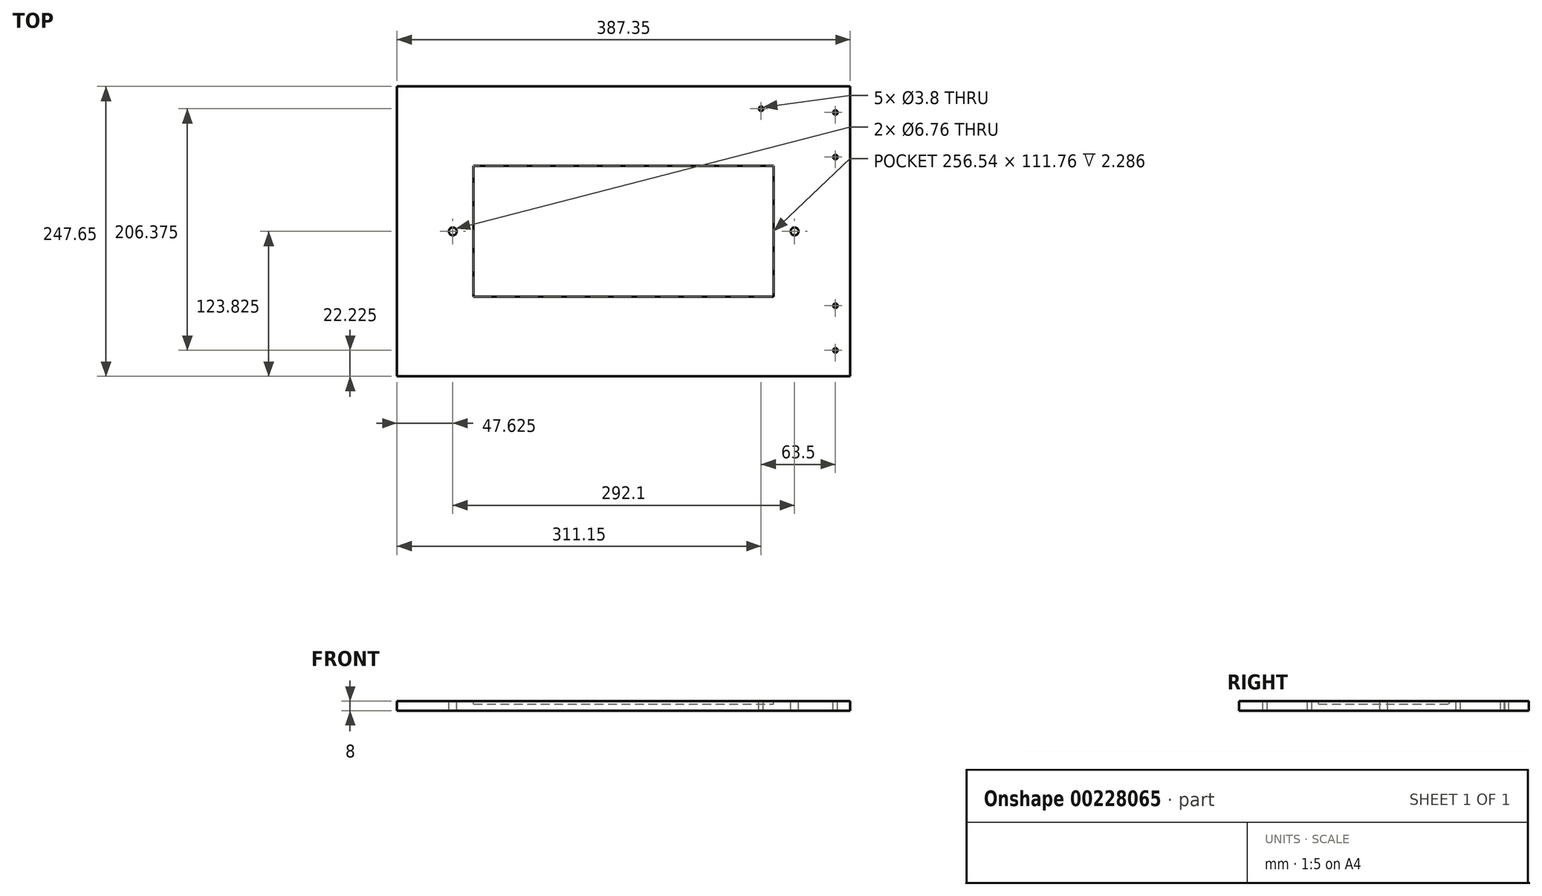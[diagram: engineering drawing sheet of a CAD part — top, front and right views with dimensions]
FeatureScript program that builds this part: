
annotation { "Feature Type Name" : "Feature", "Feature Type Description" : "" }
export const myFeature = defineFeature(function(context is Context, id is Id, definition is map)
    precondition{}
    {
        {
            var Q0;
            Q0=qCreatedBy(makeId("Top.planeOp"),FACE);
            var sketch = newSketch(context, id + "F0", { "sketchPlane" : qUnion([Q0])});
            skLineSegment(sketch, "E0.bottom", {"start": v(0, 0) * mm, "end": v(387.35, 0) * mm});
            skLineSegment(sketch, "E0.top", {"start": v(0, 247.65) * mm, "end": v(387.35, 247.65) * mm});
            skLineSegment(sketch, "E0.left", {"start": v(0, 0) * mm, "end": v(0, 247.65) * mm});
            skLineSegment(sketch, "E0.right", {"start": v(387.35, 0) * mm, "end": v(387.35, 247.65) * mm});
            skSolve(sketch);
        }
        {
            var Q0;
            Q0 = qSketchRegion(id + "F0", true);
            extrude(context, id + "F1", {"entities" : qUnion([Q0]), "depth" : 8 * mm});
        }
        {
            var Q0;
            Q0=makeQuery(id+"F1.opExtrude","CAP_FACE",FACE,{"disambiguationData":[OSD([sQuery(id+"F0.wireOp",EDGE,"E0.bottom"),sQuery(id+"F0.wireOp",EDGE,"E0.top"),sQuery(id+"F0.wireOp",EDGE,"E0.left"),sQuery(id+"F0.wireOp",EDGE,"E0.right")])],"isStart":false});
            var sketch = newSketch(context, id + "F2", { "sketchPlane" : qUnion([Q0])});
            skPoint(sketch, "E1", {"position": v(374.65, 225.43) * mm});
            skPoint(sketch, "E2", {"position": v(374.65, 187.33) * mm});
            skPoint(sketch, "E3", {"position": v(374.65, 60.33) * mm});
            skPoint(sketch, "E4", {"position": v(374.65, 22.23) * mm});
            skLineSegment(sketch, "E5", {"start": v(374.65, 225.43) * mm, "end": v(374.65, 247.65) * mm, "construction": true});
            skLineSegment(sketch, "E6", {"start": v(374.65, 22.23) * mm, "end": v(374.65, 0) * mm, "construction": true});
            skSolve(sketch);
        }
        {
            var Q0;
            Q0=sQuery(id+"F2.wireOp",VERTEX,"E1");
            var Q1;
            Q1=sQuery(id+"F2.wireOp",VERTEX,"E2");
            var Q2;
            Q2=sQuery(id+"F2.wireOp",VERTEX,"E3");
            var Q3;
            Q3=sQuery(id+"F2.wireOp",VERTEX,"E4");
            var Q4;
            Q4=makeQuery(id+"F1.opExtrude","SWEPT_BODY",BODY,{"disambiguationData":[OSD([sQuery(id+"F0.wireOp",EDGE,"E0.bottom"),sQuery(id+"F0.wireOp",EDGE,"E0.top"),sQuery(id+"F0.wireOp",EDGE,"E0.left"),sQuery(id+"F0.wireOp",EDGE,"E0.right")])]});
            hole(context, id + "F3", {"style" : HoleStyle.SIMPLE, "endStyle" : HoleEndStyle.THROUGH, "standardTappedOrClearance" : lookupTablePath({ "standard" : "ANSI", "fit" : "Normal (ASME)", "size" : "#6", "type" : "Clearance" }), "standardBlindInLast" : lookupTablePath({ "fit" : "Free", "standard" : "ANSI", "size" : "#6", "type" : "Clearance" }), "holeDiameter" : 3.8 * mm, "locations" : qUnion([Q0, Q1, Q2, Q3]), "scope" : qUnion([Q4]), "isTappedThrough" : true});
        }
        {
            var Q0;
            Q0=makeQuery(id+"F1.opExtrude","CAP_FACE",FACE,{"disambiguationData":[OSD([sQuery(id+"F0.wireOp",EDGE,"E0.bottom"),sQuery(id+"F0.wireOp",EDGE,"E0.top"),sQuery(id+"F0.wireOp",EDGE,"E0.left"),sQuery(id+"F0.wireOp",EDGE,"E0.right")])],"isStart":false});
            var sketch = newSketch(context, id + "F4", { "sketchPlane" : qUnion([Q0])});
            skPoint(sketch, "E7", {"position": v(47.62, 123.83) * mm});
            skPoint(sketch, "E8", {"position": v(339.73, 123.83) * mm});
            skLineSegment(sketch, "E9", {"start": v(47.62, 247.65) * mm, "end": v(47.62, 0) * mm, "construction": true});
            skLineSegment(sketch, "E10", {"start": v(339.73, 247.65) * mm, "end": v(339.73, 0) * mm, "construction": true});
            skLineSegment(sketch, "E11", {"start": v(0, 123.83) * mm, "end": v(47.62, 123.83) * mm, "construction": true});
            skLineSegment(sketch, "E12", {"start": v(339.73, 123.83) * mm, "end": v(387.35, 123.83) * mm, "construction": true});
            skSolve(sketch);
        }
        {
            var Q0;
            Q0=sQuery(id+"F4.wireOp",VERTEX,"E7");
            var Q1;
            Q1=sQuery(id+"F4.wireOp",VERTEX,"E8");
            var Q2;
            Q2=makeQuery(id+"F1.opExtrude","SWEPT_BODY",BODY,{"disambiguationData":[OSD([sQuery(id+"F0.wireOp",EDGE,"E0.bottom"),sQuery(id+"F0.wireOp",EDGE,"E0.top"),sQuery(id+"F0.wireOp",EDGE,"E0.left"),sQuery(id+"F0.wireOp",EDGE,"E0.right")])]});
            hole(context, id + "F5", {"style" : HoleStyle.SIMPLE, "endStyle" : HoleEndStyle.THROUGH, "standardTappedOrClearance" : lookupTablePath({ "standard" : "ANSI", "fit" : "Normal (ASME)", "size" : "1/4", "type" : "Clearance" }), "standardBlindInLast" : lookupTablePath({ "fit" : "Free", "standard" : "ANSI", "size" : "1/4", "type" : "Clearance" }), "holeDiameter" : 6.76 * mm, "locations" : qUnion([Q0, Q1]), "scope" : qUnion([Q2]), "isTappedThrough" : true});
        }
        {
            var Q0;
            Q0=makeQuery(id+"F1.opExtrude","CAP_FACE",FACE,{"disambiguationData":[OSD([sQuery(id+"F0.wireOp",EDGE,"E0.bottom"),sQuery(id+"F0.wireOp",EDGE,"E0.top"),sQuery(id+"F0.wireOp",EDGE,"E0.left"),sQuery(id+"F0.wireOp",EDGE,"E0.right")])],"isStart":false});
            var sketch = newSketch(context, id + "F6", { "sketchPlane" : qUnion([Q0])});
            skLineSegment(sketch, "E13.bottom", {"start": v(65.4, 67.95) * mm, "end": v(321.95, 67.95) * mm});
            skLineSegment(sketch, "E13.top", {"start": v(65.4, 179.7) * mm, "end": v(321.95, 179.7) * mm});
            skLineSegment(sketch, "E13.left", {"start": v(65.4, 67.95) * mm, "end": v(65.4, 179.7) * mm});
            skLineSegment(sketch, "E13.right", {"start": v(321.94, 67.95) * mm, "end": v(321.94, 179.7) * mm});
            skLineSegment(sketch, "E14", {"start": v(193.68, 247.65) * mm, "end": v(193.68, 179.7) * mm, "construction": true});
            skLineSegment(sketch, "E15", {"start": v(193.68, 67.95) * mm, "end": v(193.68, 0) * mm, "construction": true});
            skLineSegment(sketch, "E16", {"start": v(65.4, 123.83) * mm, "end": v(0, 123.83) * mm, "construction": true});
            skLineSegment(sketch, "E17", {"start": v(321.94, 123.83) * mm, "end": v(387.35, 123.83) * mm, "construction": true});
            skSolve(sketch);
        }
        {
            var Q0;
            Q0 = qSketchRegion(id + "F6", true);
            extrude(context, id + "F7", {"entities" : qUnion([Q0]), "operationType" : NewBodyOperationType.REMOVE, "oppositeDirection" : true, "depth" : 2.3 * mm});
        }
        {
            var Q0;
            Q0=makeQuery(id+"F1.opExtrude","CAP_FACE",FACE,{"disambiguationData":[OSD([sQuery(id+"F0.wireOp",EDGE,"E0.bottom"),sQuery(id+"F0.wireOp",EDGE,"E0.top"),sQuery(id+"F0.wireOp",EDGE,"E0.left"),sQuery(id+"F0.wireOp",EDGE,"E0.right")])],"isStart":false});
            var sketch = newSketch(context, id + "F8", { "sketchPlane" : qUnion([Q0])});
            skPoint(sketch, "E18", {"position": v(311.15, 228.6) * mm});
            skSolve(sketch);
        }
        {
            var Q0;
            Q0=sQuery(id+"F8.wireOp",VERTEX,"E18");
            var Q1;
            Q1=makeQuery(id+"F1.opExtrude","SWEPT_BODY",BODY,{"disambiguationData":[OSD([sQuery(id+"F0.wireOp",EDGE,"E0.bottom"),sQuery(id+"F0.wireOp",EDGE,"E0.top"),sQuery(id+"F0.wireOp",EDGE,"E0.left"),sQuery(id+"F0.wireOp",EDGE,"E0.right")])]});
            hole(context, id + "F9", {"style" : HoleStyle.SIMPLE, "endStyle" : HoleEndStyle.THROUGH, "standardTappedOrClearance" : lookupTablePath({ "standard" : "ANSI", "fit" : "Normal (ASME)", "size" : "#6", "type" : "Clearance" }), "standardBlindInLast" : lookupTablePath({ "fit" : "Free", "standard" : "ANSI", "size" : "#6", "type" : "Clearance" }), "holeDiameter" : 3.8 * mm, "locations" : qUnion([Q0]), "scope" : qUnion([Q1]), "isTappedThrough" : true});
        }
    });
